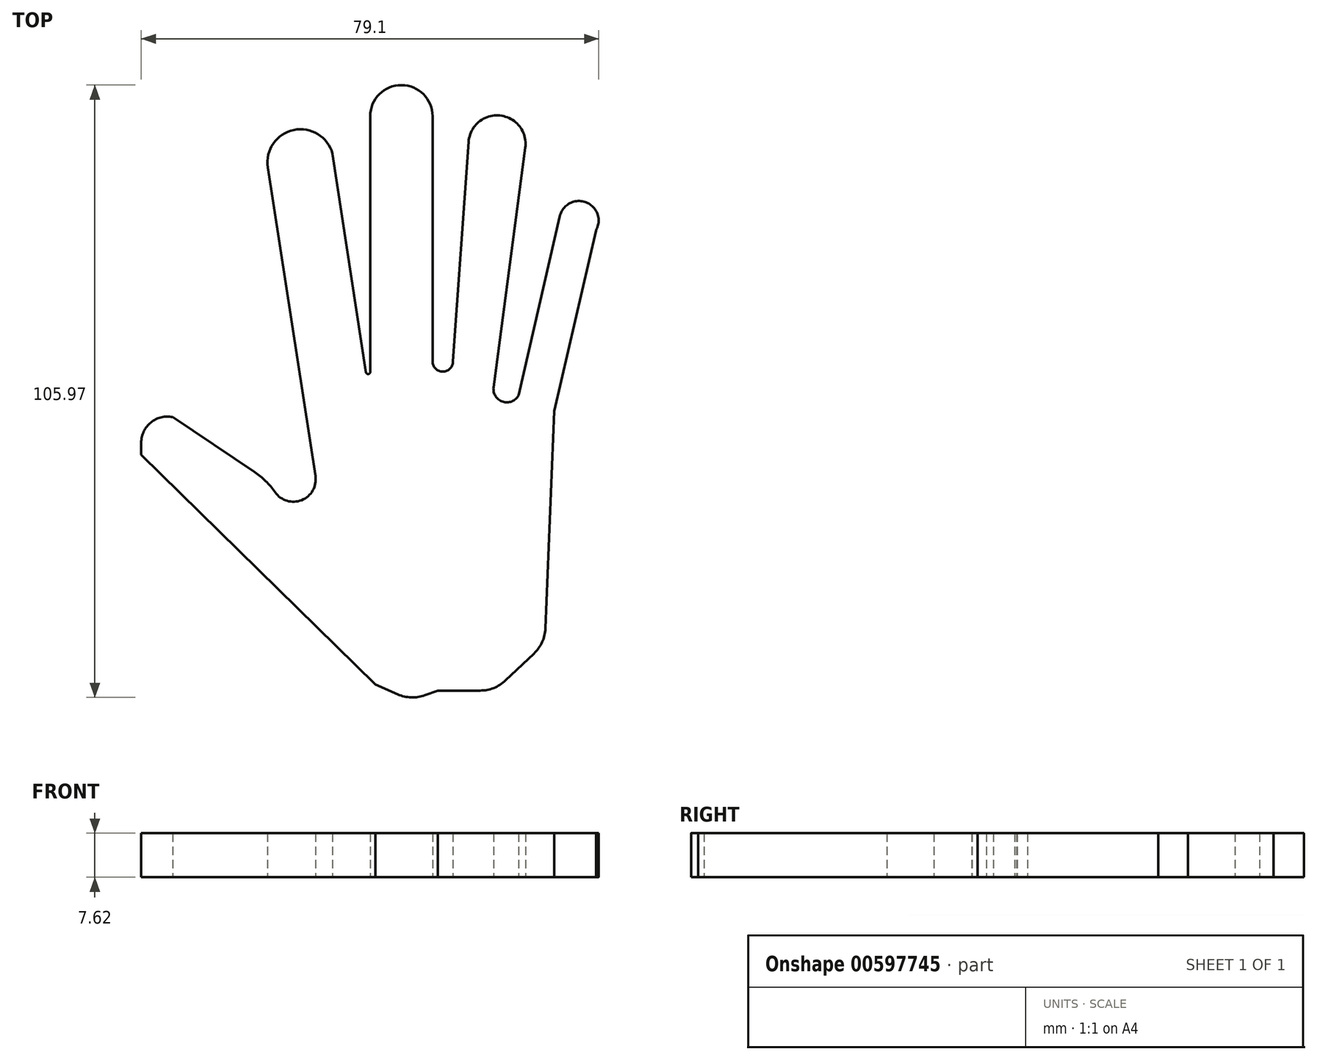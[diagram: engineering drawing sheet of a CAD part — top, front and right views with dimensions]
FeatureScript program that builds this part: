
annotation { "Feature Type Name" : "Feature", "Feature Type Description" : "" }
export const myFeature = defineFeature(function(context is Context, id is Id, definition is map)
    precondition{}
    {
        {
            var Q0;
            Q0=qCreatedBy(makeId("Top.planeOp"),FACE);
            var sketch = newSketch(context, id + "F0", { "sketchPlane" : qUnion([Q0])});
            skLineSegment(sketch, "E0", {"start": v(-34.73, 57.77) * mm, "end": v(-26.5, 4.36) * mm});
            skLineSegment(sketch, "E1", {"start": v(-23.54, 60.11) * mm, "end": v(-17.75, 22.32) * mm});
            skLineSegment(sketch, "E2", {"start": v(-17.02, 66.62) * mm, "end": v(-17.02, 22.32) * mm});
            skLineSegment(sketch, "E3", {"start": v(-6.23, 66.62) * mm, "end": v(-6.23, 24.2) * mm});
            skLineSegment(sketch, "E4", {"start": v(0, 62.2) * mm, "end": v(-2.69, 24.2) * mm});
            skLineSegment(sketch, "E5", {"start": v(9.79, 61.17) * mm, "end": v(4.31, 19.72) * mm});
            skLineSegment(sketch, "E6", {"start": v(15.79, 49.33) * mm, "end": v(8.61, 18.31) * mm});
            skLineSegment(sketch, "E7", {"start": v(22.02, 46.86) * mm, "end": v(14.8, 15.6) * mm});
            skLineSegment(sketch, "E8", {"start": v(14.8, 15.6) * mm, "end": v(13.27, -22) * mm});
            skLineSegment(sketch, "E9", {"start": v(-56.62, 8.05) * mm, "end": v(-16.14, -31.74) * mm});
            skLineSegment(sketch, "E10", {"start": v(-56.62, 8.05) * mm, "end": v(-56.62, 10.13) * mm});
            skLineSegment(sketch, "E11", {"start": v(11.3, -26.36) * mm, "end": v(6.37, -31.02) * mm});
            skLineSegment(sketch, "E12", {"start": v(2, -32.76) * mm, "end": v(-5.34, -32.76) * mm});
            skLineSegment(sketch, "E13", {"start": v(-5.34, -32.76) * mm, "end": v(-7.58, -33.57) * mm});
            skLineSegment(sketch, "E14", {"start": v(-12.26, -33.42) * mm, "end": v(-16.14, -31.74) * mm});
            skPoint(sketch, "E15.visualSharp", {"position": v(-9.95, -34.42) * mm});
            skArc(sketch, "E15.filletArc", {"start": v(-12.26, -33.42) * mm, "mid": v(-9.94, -33.94) * mm, "end": v(-7.58, -33.57) * mm});
            skPoint(sketch, "E16.visualSharp", {"position": v(4.53, -32.76) * mm});
            skArc(sketch, "E16.filletArc", {"start": v(2, -32.76) * mm, "mid": v(4.35, -32.31) * mm, "end": v(6.37, -31.02) * mm});
            skPoint(sketch, "E17.visualSharp", {"position": v(13.17, -24.58) * mm});
            skArc(sketch, "E17.filletArc", {"start": v(11.3, -26.36) * mm, "mid": v(12.7, -24.37) * mm, "end": v(13.27, -22) * mm});
            skArc(sketch, "E18", {"start": v(-17.75, 22.32) * mm, "mid": v(-17.39, 22.01) * mm, "end": v(-17.02, 22.32) * mm});
            skArc(sketch, "E19", {"start": v(-6.23, 24.2) * mm, "mid": v(-4.46, 22.43) * mm, "end": v(-2.69, 24.2) * mm});
            skArc(sketch, "E20", {"start": v(4.31, 19.72) * mm, "mid": v(5.88, 17.23) * mm, "end": v(8.61, 18.31) * mm});
            skArc(sketch, "E21", {"start": v(-26.5, 4.36) * mm, "mid": v(-28.86, 0.2) * mm, "end": v(-33.46, 1.56) * mm});
            skArc(sketch, "E22", {"start": v(-56.62, 10.13) * mm, "mid": v(-54.94, 13.65) * mm, "end": v(-51.15, 14.56) * mm});
            skLineSegment(sketch, "E23", {"start": v(-51.15, 14.56) * mm, "end": v(-37.02, 5.06) * mm});
            skPoint(sketch, "E24.visualSharp", {"position": v(-29.5, 0) * mm});
            skArc(sketch, "E24.filletArc", {"start": v(-33.46, 1.56) * mm, "mid": v(-35.08, 3.47) * mm, "end": v(-37.02, 5.06) * mm});
            skArc(sketch, "E25", {"start": v(-34.73, 57.77) * mm, "mid": v(-30.25, 64.25) * mm, "end": v(-23.54, 60.11) * mm});
            skArc(sketch, "E26", {"start": v(-17.02, 66.62) * mm, "mid": v(-11.63, 72.02) * mm, "end": v(-6.23, 66.62) * mm});
            skArc(sketch, "E27", {"start": v(0, 62.2) * mm, "mid": v(5.43, 66.75) * mm, "end": v(9.79, 61.17) * mm});
            skArc(sketch, "E28", {"start": v(15.79, 49.33) * mm, "mid": v(20.34, 51.72) * mm, "end": v(22.02, 46.86) * mm});
            skSolve(sketch);
        }
        {
            var Q0;
            Q0=makeQuery(id+"F0.imprint","IMPRINT",FACE,{"disambiguationData":[TD([[makeQuery(id+"F0.imprint","IMPRINT",EDGE,{"derivedFrom":sQuery(id+"F0.wireOp",EDGE,"E0")}),1.0]])]});
            var sketch = newSketch(context, id + "F1", { "sketchPlane" : qUnion([Q0])});
            skSolve(sketch);
        }
        {
            var Q0;
            Q0=makeQuery(id+"F0.imprint","IMPRINT",FACE,{"disambiguationData":[TD([[makeQuery(id+"F0.imprint","IMPRINT",EDGE,{"derivedFrom":sQuery(id+"F0.wireOp",EDGE,"E0")}),1.0]])]});
            var Q1;
            Q1=makeQuery(id+"F1.imprint","IMPRINT",FACE,{"disambiguationData":[TD([[makeQuery(id+"F1.imprint","IMPRINT",EDGE,{"derivedFrom":makeQuery(id+"F0.imprint","IMPRINT",EDGE,{"derivedFrom":sQuery(id+"F0.wireOp",EDGE,"E0")})}),1.0]])]});
            extrude(context, id + "F2", {"entities" : qUnion([Q0, Q1]), "depth" : 7.62 * mm, "offsetDistance" : 25.4 * mm});
        }
    });
